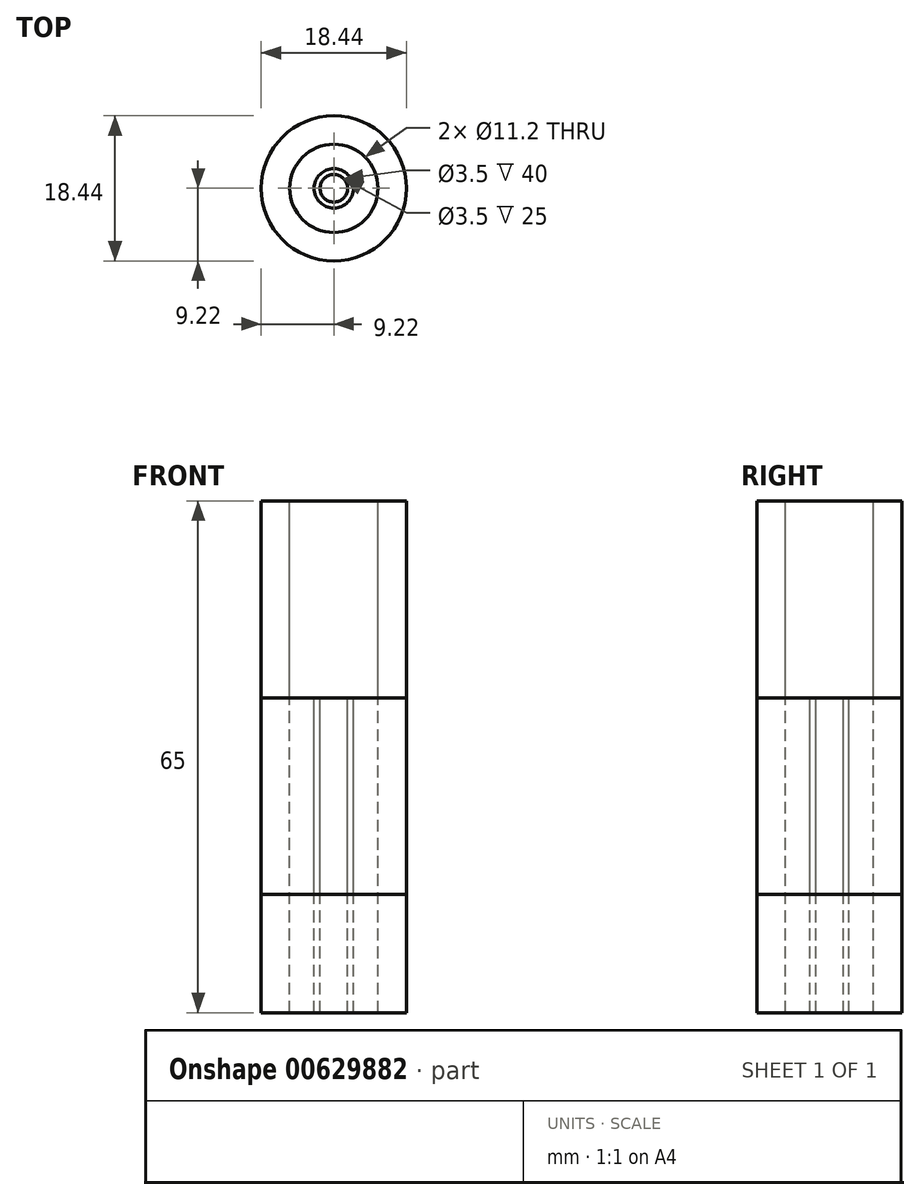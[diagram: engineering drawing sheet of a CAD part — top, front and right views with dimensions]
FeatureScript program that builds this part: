
annotation { "Feature Type Name" : "Feature", "Feature Type Description" : "" }
export const myFeature = defineFeature(function(context is Context, id is Id, definition is map)
    precondition{}
    {
        {
            var Q0;
            Q0=qCreatedBy(makeId("Top.planeOp"),FACE);
            var sketch = newSketch(context, id + "F0", { "sketchPlane" : qUnion([Q0])});
            skCircle(sketch, "E0", {"center": v(0, 0) * mm, "radius": 9.22 * mm});
            skCircle(sketch, "E1", {"center": v(0, 0) * mm, "radius": 1.75 * mm});
            skCircle(sketch, "E2", {"center": v(0, 0) * mm, "radius": 2.5 * mm});
            skCircle(sketch, "E3", {"center": v(0, 0) * mm, "radius": 5.6 * mm});
            skSolve(sketch);
        }
        {
            var Q0;
            Q0=makeQuery(id+"F0.imprint","IMPRINT",FACE,{"disambiguationData":[TD([[makeQuery(id+"F0.imprint","IMPRINT",EDGE,{"derivedFrom":sQuery(id+"F0.wireOp",EDGE,"E0")}),1.0]])]});
            var Q1;
            Q1=makeQuery(id+"F0.imprint","IMPRINT",FACE,{"disambiguationData":[TD([[makeQuery(id+"F0.imprint","IMPRINT",EDGE,{"derivedFrom":sQuery(id+"F0.wireOp",EDGE,"E2")}),-1.0]])]});
            var Q2;
            Q2=makeQuery(id+"F0.imprint","IMPRINT",FACE,{"disambiguationData":[TD([[makeQuery(id+"F0.imprint","IMPRINT",EDGE,{"derivedFrom":sQuery(id+"F0.wireOp",EDGE,"E1")}),-1.0]])]});
            var Q3;
            Q3=sQuery(id+"F0.wireOp",EDGE,"E0");
            extrude(context, id + "F1", {"entities" : qUnion([Q0, Q1, Q2]), "surfaceEntities" : qUnion([Q3]), "oppositeDirection" : true, "depth" : 40 * mm, "offsetDistance" : 25 * mm});
        }
        {
            var Q0;
            Q0=makeQuery(id+"F1.opExtrude","CAP_FACE",FACE,{"disambiguationData":[OSD([sQuery(id+"F0.wireOp",EDGE,"E0"),sQuery(id+"F0.wireOp",EDGE,"E1")])],"isStart":true});
            var sketch = newSketch(context, id + "F2", { "sketchPlane" : qUnion([Q0])});
            skCircle(sketch, "E4", {"center": v(0, 0) * mm, "radius": 7.2 * mm});
            skSolve(sketch);
        }
        {
            var Q0;
            {var subQ0=sQuery(id+"F0.wireOp",EDGE,"E1");Q0=makeQuery(id+"FgwJto66Q5EToY0_1.boolean.opBoolean","SPLIT",FACE,{"disambiguationData":[TD([makeQuery(id+"F1.opExtrude","SWEPT_FACE",FACE,{"disambiguationData":[OSD([subQ0])]})])],"derivedFrom":makeQuery(id+"F1.opExtrude","CAP_FACE",FACE,{"disambiguationData":[OSD([sQuery(id+"F0.wireOp",EDGE,"E0"),subQ0])],"isStart":true})});}
            var sketch = newSketch(context, id + "F3", { "sketchPlane" : qUnion([Q0])});
            skLineSegment(sketch, "E5", {"start": v(5.66, 0) * mm, "end": v(5.66, -5.35) * mm, "construction": true});
            skLineSegment(sketch, "E6", {"start": v(-2.86, 0) * mm, "end": v(-2.86, 4.03) * mm, "construction": true});
            skLineSegment(sketch, "E7", {"start": v(1.75, 0) * mm, "end": v(1.75, 3.7) * mm, "construction": true});
            skLineSegment(sketch, "E8", {"start": v(1.75, 3.7) * mm, "end": v(4.1, 0) * mm, "construction": true});
            skLineSegment(sketch, "E9", {"start": v(4.1, 0) * mm, "end": v(4.1, 3.87) * mm, "construction": true});
            skSolve(sketch);
        }
        {
            var Q0;
            Q0 = qSketchRegion(id + "F0", true);
            extrude(context, id + "F4", {"entities" : qUnion([Q0]), "operationType" : NewBodyOperationType.ADD, "depth" : 25 * mm, "offsetDistance" : 25 * mm});
        }
        {
            var Q0;
            Q0=makeQuery(id+"F2.imprint","IMPRINT",FACE,{"disambiguationData":[TD([[makeQuery(id+"F2.imprint","IMPRINT",EDGE,{"derivedFrom":makeQuery(id+"F1.opExtrude","CAP_EDGE",EDGE,{"disambiguationData":[OSD([sQuery(id+"F0.wireOp",EDGE,"E3")])],"isStart":true})}),1.0]])]});
            var Q1;
            Q1=makeQuery(id+"F2.imprint","IMPRINT",FACE,{"disambiguationData":[TD([[makeQuery(id+"F2.imprint","IMPRINT",EDGE,{"derivedFrom":sQuery(id+"F2.wireOp",EDGE,"E4")}),1.0]])]});
            var Q2;
            Q2=makeQuery(id+"F3.imprint","IMPRINT",FACE,{"disambiguationData":[TD([[makeQuery(id+"F3.imprint","IMPRINT",EDGE,{"derivedFrom":makeQuery(id+"F1.opExtrude","CAP_EDGE",EDGE,{"disambiguationData":[OSD([sQuery(id+"F0.wireOp",EDGE,"E0")])],"isStart":true})}),1.0]])]});
            var Q3;
            Q3=makeQuery(id+"F2.imprint","IMPRINT",FACE,{"disambiguationData":[TD([[makeQuery(id+"F2.imprint","IMPRINT",EDGE,{"derivedFrom":makeQuery(id+"F1.opExtrude","CAP_EDGE",EDGE,{"disambiguationData":[OSD([sQuery(id+"F0.wireOp",EDGE,"E1")])],"isStart":true})}),1.0]])]});
            var Q4;
            Q4=makeQuery(id+"F2.imprint","IMPRINT",FACE,{"disambiguationData":[TD([[makeQuery(id+"F2.imprint","IMPRINT",EDGE,{"derivedFrom":makeQuery(id+"F1.opExtrude","CAP_EDGE",EDGE,{"disambiguationData":[OSD([sQuery(id+"F0.wireOp",EDGE,"E1")])],"isStart":true})}),-1.0]])]});
            var Q5;
            Q5=makeQuery(id+"F2.imprint","IMPRINT",FACE,{"disambiguationData":[TD([[makeQuery(id+"F2.imprint","IMPRINT",EDGE,{"derivedFrom":sQuery(id+"F2.wireOp",EDGE,"E4")}),-1.0]])]});
            var Q6;
            Q6=makeQuery(id+"F1.opExtrude","CAP_FACE",FACE,{"disambiguationData":[OSD([sQuery(id+"F0.wireOp",EDGE,"E1"),sQuery(id+"F0.wireOp",EDGE,"E2")])],"isStart":true});
            var Q7;
            Q7=makeQuery(id+"F3.imprint","IMPRINT",FACE,{"disambiguationData":[TD([[makeQuery(id+"F3.imprint","IMPRINT",EDGE,{"derivedFrom":makeQuery(id+"F1.opExtrude","CAP_EDGE",EDGE,{"disambiguationData":[OSD([sQuery(id+"F0.wireOp",EDGE,"E1")])],"isStart":true})}),1.0]])]});
            var Q8;
            Q8=makeQuery(id+"F3.imprint","IMPRINT",FACE,{"disambiguationData":[TD([[makeQuery(id+"F3.imprint","IMPRINT",EDGE,{"derivedFrom":makeQuery(id+"F1.opExtrude","CAP_EDGE",EDGE,{"disambiguationData":[OSD([sQuery(id+"F0.wireOp",EDGE,"E3")])],"isStart":true})}),1.0]])]});
            var Q9;
            Q9=makeQuery(id+"F3.imprint","IMPRINT",FACE,{"disambiguationData":[TD([[makeQuery(id+"F3.imprint","IMPRINT",EDGE,{"derivedFrom":makeQuery(id+"F1.opExtrude","CAP_EDGE",EDGE,{"disambiguationData":[OSD([sQuery(id+"F0.wireOp",EDGE,"E1")])],"isStart":true})}),-1.0]])]});
            var Q10;
            Q10=makeQuery(id+"F4.opExtrude","CAP_FACE",FACE,{"disambiguationData":[OSD([sQuery(id+"F0.wireOp",EDGE,"E0"),sQuery(id+"F0.wireOp",EDGE,"E3")])],"isStart":false});
            extrude(context, id + "F5", {"entities" : qUnion([Q0, Q1, Q2, Q3, Q4, Q5, Q6, Q7, Q8, Q9, Q10]), "oppositeDirection" : true, "depth" : 25 * mm, "offsetDistance" : 25 * mm});
        }
    });
